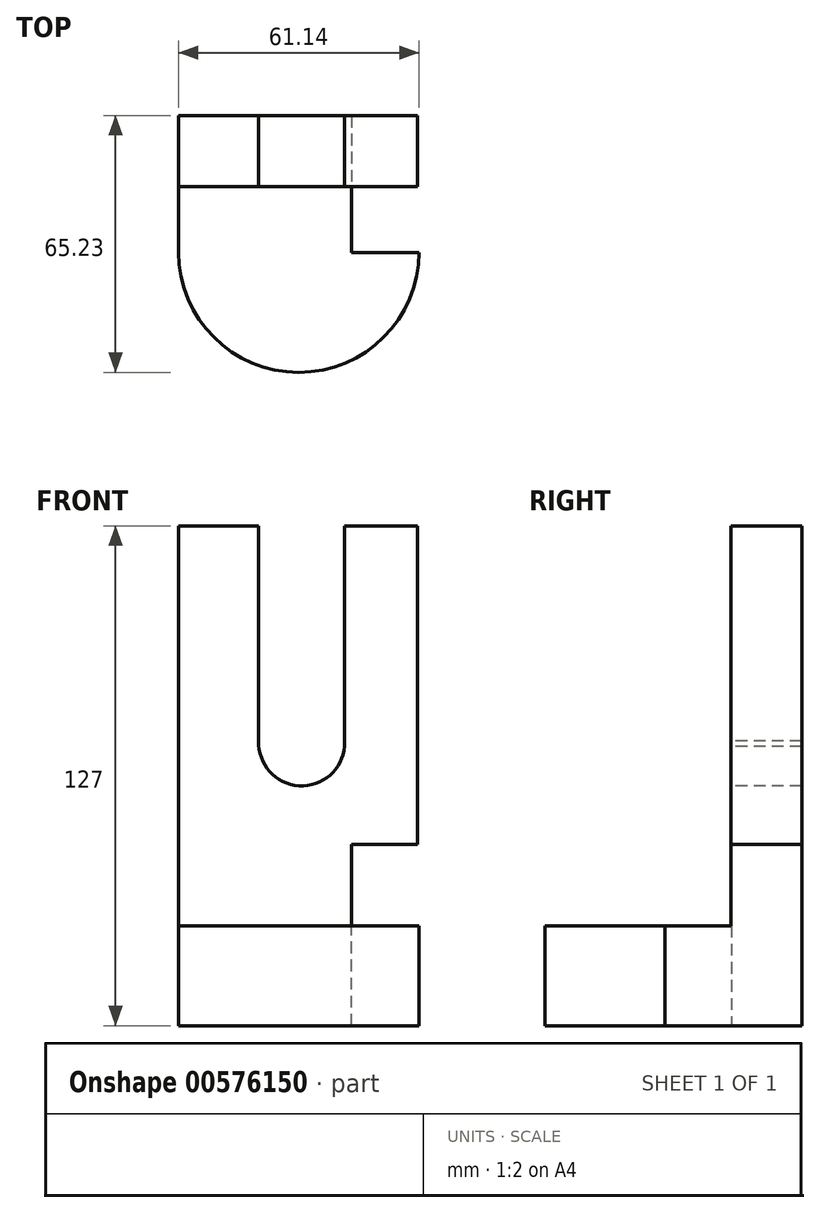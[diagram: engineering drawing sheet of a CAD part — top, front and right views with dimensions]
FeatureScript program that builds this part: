
annotation { "Feature Type Name" : "Feature", "Feature Type Description" : "" }
export const myFeature = defineFeature(function(context is Context, id is Id, definition is map)
    precondition{}
    {
        {
            var Q0;
            Q0=qCreatedBy(makeId("Top.planeOp"),FACE);
            var sketch = newSketch(context, id + "F0", { "sketchPlane" : qUnion([Q0])});
            skArc(sketch, "E0", {"start": v(-31.32, 0) * mm, "mid": v(-0.75, -30.43) * mm, "end": v(29.82, 0) * mm});
            skLineSegment(sketch, "E1", {"start": v(-31.32, 0) * mm, "end": v(29.82, 0) * mm});
            skSolve(sketch);
        }
        {
            var Q0;
            Q0 = qSketchRegion(id + "F0", true);
            extrude(context, id + "F1", {"entities" : qUnion([Q0]), "depth" : 25.4 * mm, "offsetDistance" : 25.4 * mm});
        }
        {
            var Q0;
            Q0=qCreatedBy(makeId("Top.planeOp"),FACE);
            var sketch = newSketch(context, id + "F2", { "sketchPlane" : qUnion([Q0])});
            skLineSegment(sketch, "E2.bottom", {"start": v(29.65, 0) * mm, "end": v(-31.32, 0) * mm});
            skLineSegment(sketch, "E2.top", {"start": v(29.65, 16.95) * mm, "end": v(-31.32, 16.95) * mm});
            skLineSegment(sketch, "E2.left", {"start": v(29.65, 0) * mm, "end": v(29.65, 16.95) * mm});
            skLineSegment(sketch, "E2.right", {"start": v(-31.32, 0) * mm, "end": v(-31.32, 16.95) * mm});
            skSolve(sketch);
        }
        {
            var Q0;
            Q0 = qSketchRegion(id + "F2", true);
            extrude(context, id + "F3", {"entities" : qUnion([Q0]), "operationType" : NewBodyOperationType.ADD, "depth" : 25.4 * mm, "offsetDistance" : 25.4 * mm});
        }
        {
            var Q0;
            Q0=makeQuery(id+"F3.boolean.opBoolean","MERGE",FACE,{"derivedFrom":[makeQuery(id+"F1.opExtrude","CAP_FACE",FACE,{"disambiguationData":[OSD([sQuery(id+"F0.wireOp",EDGE,"E0"),sQuery(id+"F0.wireOp",EDGE,"E1")])],"isStart":false}),makeQuery(id+"F3.opExtrude","CAP_FACE",FACE,{"disambiguationData":[OSD([sQuery(id+"F2.wireOp",EDGE,"E2.bottom"),sQuery(id+"F2.wireOp",EDGE,"E2.top"),sQuery(id+"F2.wireOp",EDGE,"E2.left"),sQuery(id+"F2.wireOp",EDGE,"E2.right")])],"isStart":false})]});
            var sketch = newSketch(context, id + "F4", { "sketchPlane" : qUnion([Q0])});
            skLineSegment(sketch, "E3.bottom", {"start": v(12.71, 16.95) * mm, "end": v(29.82, 16.95) * mm});
            skLineSegment(sketch, "E3.top", {"start": v(12.71, 0) * mm, "end": v(29.82, 0) * mm});
            skLineSegment(sketch, "E3.left", {"start": v(12.71, 16.95) * mm, "end": v(12.71, 0) * mm});
            skLineSegment(sketch, "E3.right", {"start": v(29.82, 16.95) * mm, "end": v(29.82, 0) * mm});
            skSolve(sketch);
        }
        {
            var Q0;
            Q0 = qSketchRegion(id + "F4", true);
            extrude(context, id + "F5", {"entities" : qUnion([Q0]), "operationType" : NewBodyOperationType.REMOVE, "oppositeDirection" : true, "depth" : 25.4 * mm, "offsetDistance" : 25.4 * mm});
        }
        {
            var Q0;
            Q0=qCreatedBy(makeId("Top.planeOp"),FACE);
            var sketch = newSketch(context, id + "F6", { "sketchPlane" : qUnion([Q0])});
            skLineSegment(sketch, "E4.bottom", {"start": v(-31.27, 16.82) * mm, "end": v(29.41, 16.82) * mm});
            skLineSegment(sketch, "E4.top", {"start": v(-31.27, 34.8) * mm, "end": v(29.41, 34.8) * mm});
            skLineSegment(sketch, "E4.left", {"start": v(-31.27, 16.82) * mm, "end": v(-31.27, 34.8) * mm});
            skLineSegment(sketch, "E4.right", {"start": v(29.41, 16.82) * mm, "end": v(29.41, 34.8) * mm});
            skSolve(sketch);
        }
        {
            var Q0;
            Q0 = qSketchRegion(id + "F6", true);
            extrude(context, id + "F7", {"entities" : qUnion([Q0]), "operationType" : NewBodyOperationType.ADD, "depth" : 127 * mm, "offsetDistance" : 25.4 * mm});
        }
        {
            var Q0;
            Q0=makeQuery(id+"F7.opExtrude","SWEPT_FACE",FACE,{"disambiguationData":[OSD([sQuery(id+"F6.wireOp",EDGE,"E4.bottom")])]});
            var sketch = newSketch(context, id + "F8", { "sketchPlane" : qUnion([Q0])});
            skLineSegment(sketch, "E5.bottom", {"start": v(12.71, 25.4) * mm, "end": v(29.41, 25.4) * mm});
            skLineSegment(sketch, "E5.top", {"start": v(12.71, 0) * mm, "end": v(29.41, 0) * mm});
            skLineSegment(sketch, "E5.left", {"start": v(12.71, 25.4) * mm, "end": v(12.71, 0) * mm});
            skLineSegment(sketch, "E5.right", {"start": v(29.41, 25.4) * mm, "end": v(29.41, 0) * mm});
            skLineSegment(sketch, "E6.bottom", {"start": v(29.41, 25.4) * mm, "end": v(12.71, 25.4) * mm});
            skLineSegment(sketch, "E6.top", {"start": v(29.41, 46.06) * mm, "end": v(12.71, 46.06) * mm});
            skLineSegment(sketch, "E6.left", {"start": v(29.41, 25.4) * mm, "end": v(29.41, 46.06) * mm});
            skLineSegment(sketch, "E6.right", {"start": v(12.71, 25.4) * mm, "end": v(12.71, 46.06) * mm});
            skSolve(sketch);
        }
        {
            var Q0;
            Q0 = qSketchRegion(id + "F8", true);
            extrude(context, id + "F9", {"entities" : qUnion([Q0]), "operationType" : NewBodyOperationType.REMOVE, "oppositeDirection" : true, "depth" : 25.4 * mm, "offsetDistance" : 25.4 * mm});
        }
        {
            var Q0;
            Q0=makeQuery(id+"F7.opExtrude","SWEPT_FACE",FACE,{"disambiguationData":[OSD([sQuery(id+"F6.wireOp",EDGE,"E4.bottom")])]});
            var sketch = newSketch(context, id + "F10", { "sketchPlane" : qUnion([Q0])});
            skArc(sketch, "E7", {"start": v(-10.91, 72.34) * mm, "mid": v(-0.67, 60.95) * mm, "end": v(10.89, 71) * mm});
            skLineSegment(sketch, "E8", {"start": v(-10.91, 72.34) * mm, "end": v(-10.91, 127) * mm});
            skLineSegment(sketch, "E9", {"start": v(10.89, 71) * mm, "end": v(10.89, 127) * mm});
            skLineSegment(sketch, "E10", {"start": v(10.89, 127) * mm, "end": v(-10.91, 127) * mm});
            skSolve(sketch);
        }
        {
            var Q0;
            Q0 = qSketchRegion(id + "F10", true);
            extrude(context, id + "F11", {"entities" : qUnion([Q0]), "operationType" : NewBodyOperationType.REMOVE, "oppositeDirection" : true, "depth" : 25.4 * mm, "offsetDistance" : 25.4 * mm});
        }
    });
